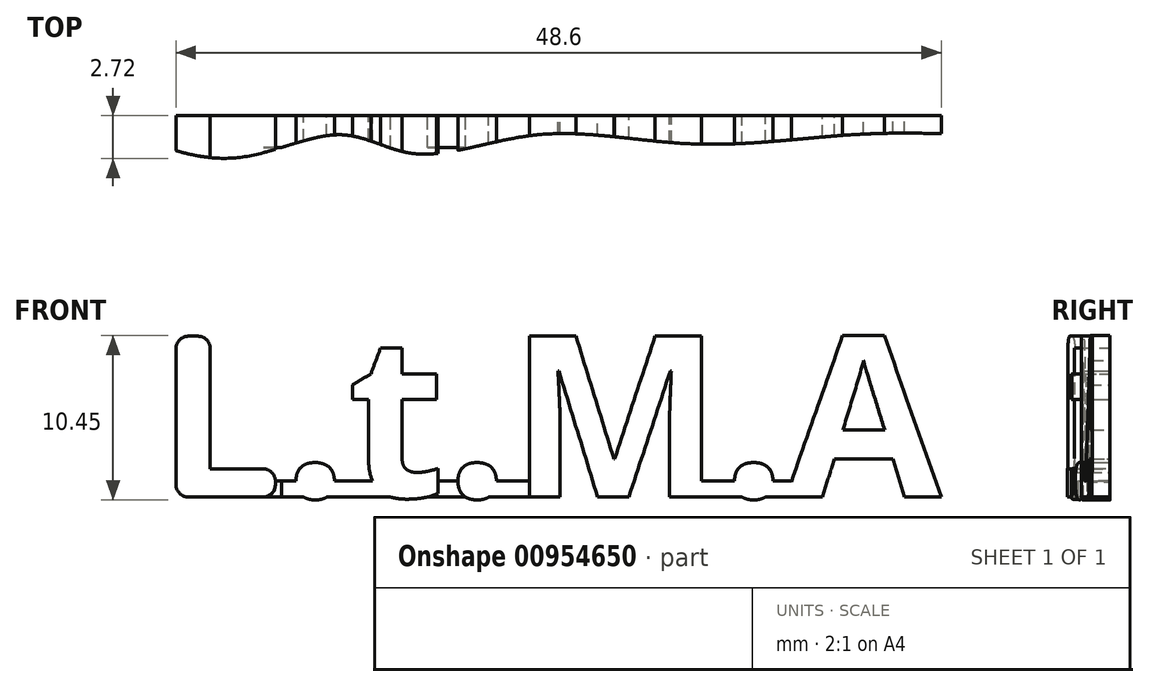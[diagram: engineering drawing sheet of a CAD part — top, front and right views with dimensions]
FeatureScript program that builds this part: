
annotation { "Feature Type Name" : "Feature", "Feature Type Description" : "" }
export const myFeature = defineFeature(function(context is Context, id is Id, definition is map)
    precondition{}
    {
        {
            var Q0;
            Q0=qCreatedBy(makeId("Front.planeOp"),FACE);
            var sketch = newSketch(context, id + "F0", { "sketchPlane" : qUnion([Q0])});
            skText(sketch, "E0", { "text": "L.t.M.A", "fontName": "OpenSans-Bold.ttf"});
            const initialGuessF0  = {"E0": [-0.02593, -0.00351, 1, 0, 0.0103]};
            skSetInitialGuess(sketch, initialGuessF0);
            skSolve(sketch);
        }
        {
            var Q0;
            Q0=makeQuery(id+"F0.imprint","IMPRINT",FACE,{"disambiguationData":[TD([[makeQuery(id+"F0.imprint","IMPRINT",EDGE,{"derivedFrom":sQuery(id+"F0.wireOp",EDGE,"E0.sketch_text.stroke-0")}),-1.0]])]});
            var Q1;
            Q1=makeQuery(id+"F0.imprint","IMPRINT",FACE,{"disambiguationData":[TD([[makeQuery(id+"F0.imprint","IMPRINT",EDGE,{"derivedFrom":sQuery(id+"F0.wireOp",EDGE,"E0.sketch_text.stroke-6")}),-1.0]])]});
            var Q2;
            Q2=makeQuery(id+"F0.imprint","IMPRINT",FACE,{"disambiguationData":[TD([[makeQuery(id+"F0.imprint","IMPRINT",EDGE,{"derivedFrom":sQuery(id+"F0.wireOp",EDGE,"E0.sketch_text.stroke-14")}),-1.0]])]});
            var Q3;
            Q3=makeQuery(id+"F0.imprint","IMPRINT",FACE,{"disambiguationData":[TD([[makeQuery(id+"F0.imprint","IMPRINT",EDGE,{"derivedFrom":sQuery(id+"F0.wireOp",EDGE,"E0.sketch_text.stroke-32")}),-1.0]])]});
            var Q4;
            Q4=makeQuery(id+"F0.imprint","IMPRINT",FACE,{"disambiguationData":[TD([[makeQuery(id+"F0.imprint","IMPRINT",EDGE,{"derivedFrom":sQuery(id+"F0.wireOp",EDGE,"E0.sketch_text.stroke-59")}),-1.0]])]});
            var Q5;
            Q5=makeQuery(id+"F0.imprint","IMPRINT",FACE,{"disambiguationData":[TD([[makeQuery(id+"F0.imprint","IMPRINT",EDGE,{"derivedFrom":sQuery(id+"F0.wireOp",EDGE,"E0.sketch_text.stroke-67")}),-1.0]])]});
            var Q6;
            Q6=makeQuery(id+"F0.imprint","IMPRINT",FACE,{"disambiguationData":[TD([[makeQuery(id+"F0.imprint","IMPRINT",EDGE,{"derivedFrom":sQuery(id+"F0.wireOp",EDGE,"E0.sketch_text.stroke-40")}),-1.0]])]});
            extrude(context, id + "F1", {"entities" : qUnion([Q0, Q1, Q2, Q3, Q4, Q5, Q6]), "depth" : 3.17 * mm, "offsetDistance" : 25.4 * mm});
        }
        {
            var Q0;
            Q0=qCreatedBy(makeId("Front.planeOp"),FACE);
            var sketch = newSketch(context, id + "F2", { "sketchPlane" : qUnion([Q0])});
            skLineSegment(sketch, "E1.bottom", {"start": v(-18.34, -2.5) * mm, "end": v(-11.03, -2.5) * mm});
            skLineSegment(sketch, "E1.top", {"start": v(-18.34, -3.51) * mm, "end": v(-11.03, -3.51) * mm});
            skLineSegment(sketch, "E1.left", {"start": v(-18.34, -2.5) * mm, "end": v(-18.34, -3.51) * mm});
            skLineSegment(sketch, "E1.right", {"start": v(-11.03, -2.5) * mm, "end": v(-11.03, -3.51) * mm});
            skLineSegment(sketch, "E2.bottom", {"start": v(-8.67, -2.5) * mm, "end": v(-2.2, -2.5) * mm});
            skLineSegment(sketch, "E2.top", {"start": v(-8.67, -3.51) * mm, "end": v(-2.2, -3.51) * mm});
            skLineSegment(sketch, "E2.left", {"start": v(-8.67, -2.5) * mm, "end": v(-8.67, -3.51) * mm});
            skLineSegment(sketch, "E2.right", {"start": v(-2.2, -2.5) * mm, "end": v(-2.2, -3.51) * mm});
            skLineSegment(sketch, "E3.bottom", {"start": v(8.7, -2.5) * mm, "end": v(14.43, -2.5) * mm});
            skLineSegment(sketch, "E3.top", {"start": v(8.7, -3.51) * mm, "end": v(14.43, -3.51) * mm});
            skLineSegment(sketch, "E3.left", {"start": v(8.7, -2.5) * mm, "end": v(8.7, -3.51) * mm});
            skLineSegment(sketch, "E3.right", {"start": v(14.43, -2.5) * mm, "end": v(14.43, -3.51) * mm});
            skSolve(sketch);
        }
        {
            var Q0;
            Q0 = qSketchRegion(id + "F2", true);
            extrude(context, id + "F3", {"entities" : qUnion([Q0]), "operationType" : NewBodyOperationType.ADD, "depth" : 2.03 * mm, "offsetDistance" : 25.4 * mm});
        }
        {
            var Q0;
            Q0=qCreatedBy(makeId("Top.planeOp"),FACE);
            var sketch = newSketch(context, id + "F4", { "sketchPlane" : qUnion([Q0])});
            skArc(sketch, "E4", {"start": v(-27.56, -1.22) * mm, "mid": v(-1.2, -3.06) * mm, "end": v(25.16, -1.19) * mm, "construction": true});
            skLineSegment(sketch, "E5", {"start": v(-27.56, -1.22) * mm, "end": v(-27.56, -4.96) * mm});
            skLineSegment(sketch, "E6", {"start": v(-27.56, -4.96) * mm, "end": v(25.32, -4.96) * mm});
            skLineSegment(sketch, "E7", {"start": v(25.32, -4.96) * mm, "end": v(25.16, -1.19) * mm});
            skFitSpline(sketch, "E8", {"points": [v(-27.56, -1.22) * mm, v(-20.77, -2.68) * mm, v(-14.18, -1.22) * mm, v(-9.43, -2.43) * mm, v(-1.68, -1.22) * mm, v(8.23, -1.8) * mm, v(18.25, -1.22) * mm, v(25.16, -1.19) * mm], "startDerivative": vector(48.9, -18.47) * mm, "endDerivative": vector(48.01, -1.38) * mm});
            skSolve(sketch);
        }
        {
            var Q0;
            Q0 = qSketchRegion(id + "F4", true);
            extrude(context, id + "F5", {"entities" : qUnion([Q0]), "operationType" : NewBodyOperationType.REMOVE, "endBound" : BoundingType.THROUGH_ALL, "oppositeDirection" : true, "depth" : 25.4 * mm, "offsetDistance" : 25.4 * mm, "hasSecondDirection" : true, "secondDirectionBound" : SecondDirectionBoundingType.THROUGH_ALL, "secondDirectionOppositeDirection" : false, "secondDirectionDepth" : 25.4 * mm});
        }
        {
            var Q0;
            Q0=makeQuery(id+"F1.opExtrude","CAP_FACE",FACE,{"disambiguationData":[OSD([sQuery(id+"F0.wireOp",EDGE,"E0.sketch_text.stroke-0"),sQuery(id+"F0.wireOp",EDGE,"E0.sketch_text.stroke-1"),sQuery(id+"F0.wireOp",EDGE,"E0.sketch_text.stroke-2"),sQuery(id+"F0.wireOp",EDGE,"E0.sketch_text.stroke-3"),sQuery(id+"F0.wireOp",EDGE,"E0.sketch_text.stroke-4"),sQuery(id+"F0.wireOp",EDGE,"E0.sketch_text.stroke-5")])],"isStart":false});
            var Q1;
            Q1=makeQuery(id+"F1.opExtrude","SWEPT_EDGE",EDGE,{"disambiguationData":[OSD([sQuery(id+"F0.wireOp",EDGE,"E0.sketch_text.stroke-0"),sQuery(id+"F0.wireOp",EDGE,"E0.sketch_text.stroke-5")])]});
            var Q2;
            Q2=makeQuery(id+"F1.opExtrude","SWEPT_EDGE",EDGE,{"disambiguationData":[OSD([sQuery(id+"F0.wireOp",EDGE,"E0.sketch_text.stroke-0"),sQuery(id+"F0.wireOp",EDGE,"E0.sketch_text.stroke-1")])]});
            var Q3;
            Q3=makeQuery(id+"F1.opExtrude","SWEPT_EDGE",EDGE,{"disambiguationData":[OSD([sQuery(id+"F0.wireOp",EDGE,"E0.sketch_text.stroke-4"),sQuery(id+"F0.wireOp",EDGE,"E0.sketch_text.stroke-5")])]});
            var Q4;
            Q4=makeQuery(id+"F1.opExtrude","SWEPT_EDGE",EDGE,{"disambiguationData":[OSD([sQuery(id+"F0.wireOp",EDGE,"E0.sketch_text.stroke-3"),sQuery(id+"F0.wireOp",EDGE,"E0.sketch_text.stroke-4")])]});
            var Q5;
            Q5=makeQuery(id+"F1.opExtrude","SWEPT_EDGE",EDGE,{"disambiguationData":[OSD([sQuery(id+"F0.wireOp",EDGE,"E0.sketch_text.stroke-1"),sQuery(id+"F0.wireOp",EDGE,"E0.sketch_text.stroke-2")])]});
            fillet(context, id + "F6", {"entities" : qUnion([Q0, Q1, Q2, Q3, Q4, Q5]), "radius" : 0.76 * mm, "tangentPropagation" : true, "allowEdgeOverflow" : false});
        }
    });
